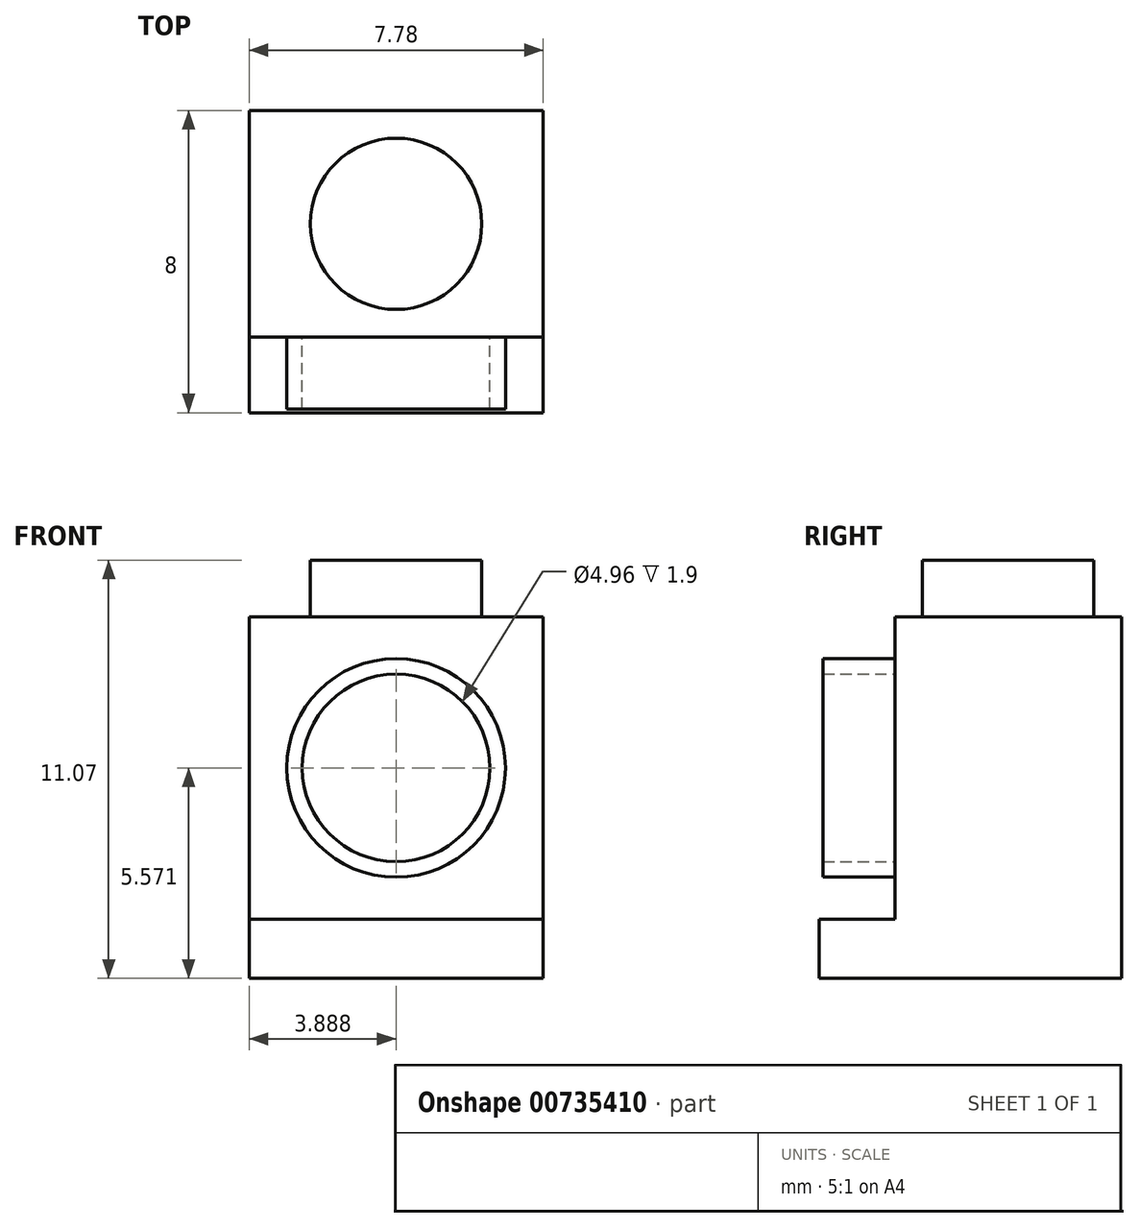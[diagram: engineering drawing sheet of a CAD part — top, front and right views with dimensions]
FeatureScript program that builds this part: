
annotation { "Feature Type Name" : "Feature", "Feature Type Description" : "" }
export const myFeature = defineFeature(function(context is Context, id is Id, definition is map)
    precondition{}
    {
        {
            var Q0;
            Q0=qCreatedBy(makeId("Front.planeOp"),FACE);
            var sketch = newSketch(context, id + "F0", { "sketchPlane" : qUnion([Q0])});
            skLineSegment(sketch, "E0", {"start": v(0, 0) * mm, "end": v(0, 1.57) * mm});
            skLineSegment(sketch, "E1", {"start": v(0, 1.57) * mm, "end": v(7.78, 1.57) * mm});
            skLineSegment(sketch, "E2", {"start": v(7.78, 1.57) * mm, "end": v(7.78, 0) * mm});
            skLineSegment(sketch, "E3", {"start": v(7.78, 0) * mm, "end": v(0, 0) * mm});
            skSolve(sketch);
        }
        {
            var Q0;
            Q0 = qSketchRegion(id + "F0", true);
            extrude(context, id + "F1", {"entities" : qUnion([Q0]), "depth" : 8 * mm, "offsetDistance" : 25 * mm});
        }
        {
            var Q0;
            Q0=makeQuery(id+"F1.opExtrude","SWEPT_FACE",FACE,{"disambiguationData":[OSD([sQuery(id+"F0.wireOp",EDGE,"E1")])]});
            var sketch = newSketch(context, id + "F2", { "sketchPlane" : qUnion([Q0])});
            skLineSegment(sketch, "E4", {"start": v(0, 0) * mm, "end": v(0, -6) * mm});
            skLineSegment(sketch, "E5", {"start": v(0, -6) * mm, "end": v(7.78, -6) * mm});
            skLineSegment(sketch, "E6", {"start": v(7.78, -6) * mm, "end": v(7.78, 0) * mm});
            skLineSegment(sketch, "E7", {"start": v(7.78, 0) * mm, "end": v(0, 0) * mm});
            skSolve(sketch);
        }
        {
            var Q0;
            Q0 = qSketchRegion(id + "F2", true);
            extrude(context, id + "F3", {"entities" : qUnion([Q0]), "operationType" : NewBodyOperationType.ADD, "depth" : 8 * mm, "offsetDistance" : 25 * mm});
        }
        {
            var Q0;
            Q0=makeQuery(id+"F3.opExtrude","SWEPT_FACE",FACE,{"disambiguationData":[OSD([sQuery(id+"F2.wireOp",EDGE,"E5")])]});
            var sketch = newSketch(context, id + "F4", { "sketchPlane" : qUnion([Q0])});
            skPoint(sketch, "E8.endSnap0", {"position": v(7.78, 5.57) * mm});
            skCircle(sketch, "E9", {"center": v(3.89, 5.57) * mm, "radius": 2.48 * mm});
            skCircle(sketch, "E10", {"center": v(3.89, 5.57) * mm, "radius": 2.9 * mm});
            skSolve(sketch);
        }
        {
            var Q0;
            Q0 = qSketchRegion(id + "F4", true);
            extrude(context, id + "F5", {"entities" : qUnion([Q0]), "operationType" : NewBodyOperationType.ADD, "depth" : 1.9 * mm, "offsetDistance" : 25 * mm});
        }
        {
            var Q0;
            Q0=makeQuery(id+"F3.opExtrude","CAP_FACE",FACE,{"disambiguationData":[OSD([sQuery(id+"F2.wireOp",EDGE,"E4"),sQuery(id+"F2.wireOp",EDGE,"E5"),sQuery(id+"F2.wireOp",EDGE,"E6"),sQuery(id+"F2.wireOp",EDGE,"E7")])],"isStart":false});
            var sketch = newSketch(context, id + "F6", { "sketchPlane" : qUnion([Q0])});
            skPoint(sketch, "E11.endSnap0", {"position": v(7.78, -3) * mm});
            skCircle(sketch, "E12", {"center": v(3.89, -3) * mm, "radius": 2.27 * mm});
            skSolve(sketch);
        }
        {
            var Q0;
            Q0 = qSketchRegion(id + "F6", true);
            extrude(context, id + "F7", {"entities" : qUnion([Q0]), "operationType" : NewBodyOperationType.ADD, "depth" : 1.5 * mm, "offsetDistance" : 25 * mm});
        }
    });
